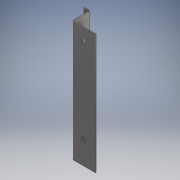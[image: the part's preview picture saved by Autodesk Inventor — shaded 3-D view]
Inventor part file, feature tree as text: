
AUTODESK INVENTOR PART (.ipt)
format: ipt  version: 2017 (Build 210142000, 142)  size: 159,232 bytes
history: native  units: mm
features: sheet_metal_op x3, sketch x2, other x2, extrude x1
ambient origin geometry x8: Origin, YZ Plane, XZ Plane, XY Plane, X Axis, Y Axis, Z Axis, Center Point
bodies: Solid1 (feature_tree)
feature tree (8):
  sheet_metal_op  "Contour Flange1"
  extrude  "Extrusion1"  Depth=37.0mm
  sketch  "Sketch1"  dims[d0=50.0mm d1=37.0mm]
  other  "Plate1"
  sheet_metal_op  "Bend1"
  sheet_metal_op  "Corner1"
  sketch  "Sketch2"  dims[d2=11.5mm d3=1.5mm d4=0.75mm d5=3.0mm d6=1.5mm d7=258.0mm d8=1.5mm d9=0.5mm d10=6.0mm d11=1.5mm d12=1.5mm d13=9.525mm d14=9.525mm d15=25.0mm d16=25.0mm d17=25.0mm d18=50.0mm d19=10.0mm d20=0.0mm]
  other  "Definition1"
